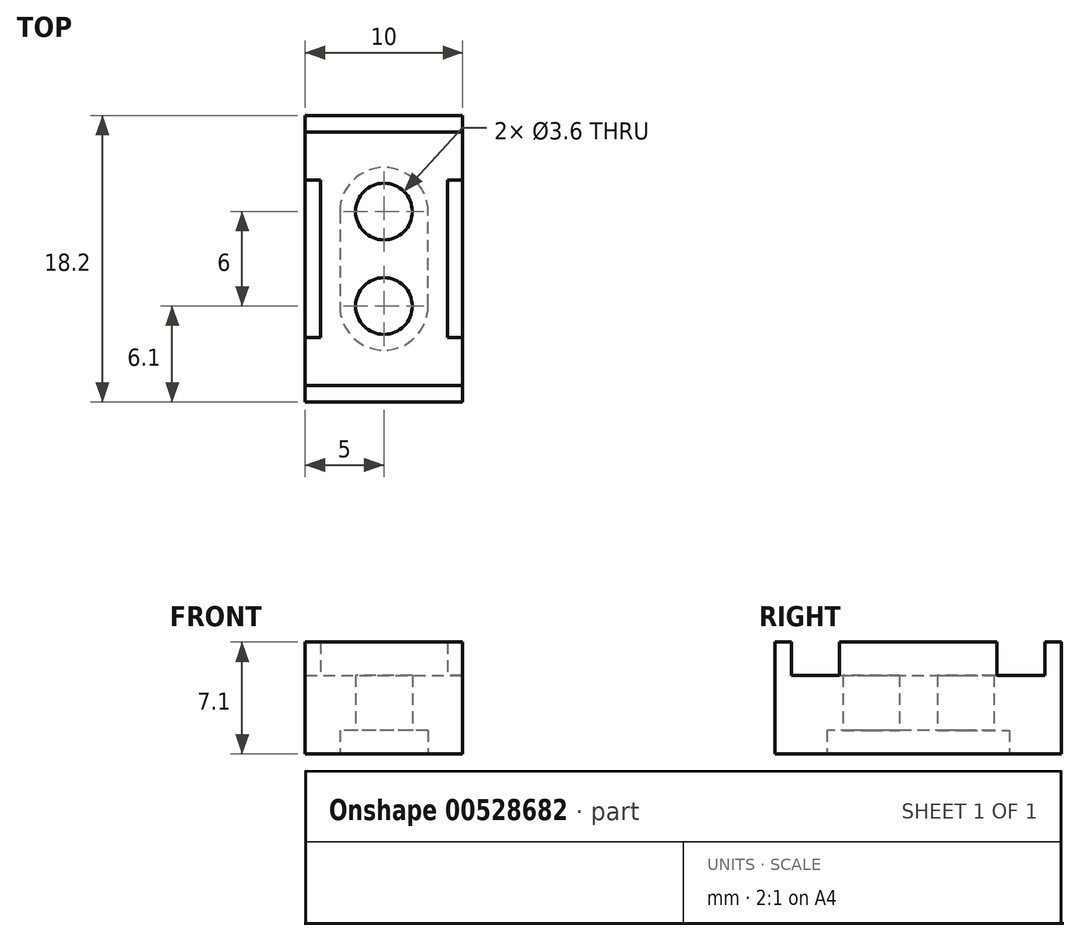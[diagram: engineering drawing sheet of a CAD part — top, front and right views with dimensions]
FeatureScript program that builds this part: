
annotation { "Feature Type Name" : "Feature", "Feature Type Description" : "" }
export const myFeature = defineFeature(function(context is Context, id is Id, definition is map)
    precondition{}
    {
        {
            var Q0;
            Q0=qCreatedBy(makeId("Top.planeOp"),FACE);
            var sketch = newSketch(context, id + "F0", { "sketchPlane" : qUnion([Q0])});
            skLineSegment(sketch, "E0.bottom", {"start": v(5, 9.1) * mm, "end": v(-5, 9.1) * mm});
            skLineSegment(sketch, "E0.top", {"start": v(5, -9.1) * mm, "end": v(-5, -9.1) * mm});
            skLineSegment(sketch, "E0.left", {"start": v(5, 9.1) * mm, "end": v(5, -9.1) * mm});
            skLineSegment(sketch, "E0.right", {"start": v(-5, 9.1) * mm, "end": v(-5, -9.1) * mm});
            skPoint(sketch, "E0.middle", {"position": v(0, 0) * mm});
            skLineSegment(sketch, "E1", {"start": v(0, 0) * mm, "end": v(0, 3) * mm, "construction": true});
            skCircle(sketch, "E2", {"center": v(0, 3) * mm, "radius": 1.8 * mm});
            skArc(sketch, "E3", {"start": v(2.8, 3) * mm, "mid": v(0, 5.8) * mm, "end": v(-2.8, 3) * mm});
            skLineSegment(sketch, "E4", {"start": v(-2.8, 3) * mm, "end": v(-2.8, 0) * mm});
            skLineSegment(sketch, "E5", {"start": v(2.8, 3) * mm, "end": v(2.8, 0) * mm});
            skArc(sketch, "E6.MirrorCS", {"start": v(2.8, -3) * mm, "mid": v(0, -5.8) * mm, "end": v(-2.8, -3) * mm});
            skLineSegment(sketch, "E7.MirrorCS", {"start": v(-2.8, -3) * mm, "end": v(-2.8, 0) * mm});
            skLineSegment(sketch, "E8.MirrorCS", {"start": v(2.8, -3) * mm, "end": v(2.8, 0) * mm});
            skCircle(sketch, "E9.MirrorC", {"center": v(0, -3) * mm, "radius": 1.8 * mm});
            skLineSegment(sketch, "E10.bottom", {"start": v(4.03, 8.05) * mm, "end": v(-4.03, 8.05) * mm});
            skLineSegment(sketch, "E10.top", {"start": v(4.03, -8.05) * mm, "end": v(-4.03, -8.05) * mm});
            skLineSegment(sketch, "E10.left", {"start": v(4.03, 8.05) * mm, "end": v(4.03, -8.05) * mm});
            skLineSegment(sketch, "E10.right", {"start": v(-4.03, 8.05) * mm, "end": v(-4.03, -8.05) * mm});
            skLineSegment(sketch, "E11", {"start": v(0, 0) * mm, "end": v(0, -5) * mm, "construction": true});
            skLineSegment(sketch, "E12", {"start": v(-4.03, -8.05) * mm, "end": v(-5, -8.05) * mm});
            skLineSegment(sketch, "E13", {"start": v(-4.03, -5) * mm, "end": v(-5, -5) * mm});
            skLineSegment(sketch, "E14.MirrorCS", {"start": v(4.03, -8.05) * mm, "end": v(5, -8.05) * mm});
            skLineSegment(sketch, "E15.MirrorCS", {"start": v(4.03, -5) * mm, "end": v(5, -5) * mm});
            skLineSegment(sketch, "E16.MirrorCS", {"start": v(4.03, 5) * mm, "end": v(5, 5) * mm});
            skLineSegment(sketch, "E17.MirrorCS", {"start": v(4.03, 8.05) * mm, "end": v(5, 8.05) * mm});
            skLineSegment(sketch, "E18.MirrorCS", {"start": v(-4.03, 5) * mm, "end": v(-5, 5) * mm});
            skLineSegment(sketch, "E19.MirrorCS", {"start": v(-4.03, 8.05) * mm, "end": v(-5, 8.05) * mm});
            skSolve(sketch);
        }
        {
            var Q0;
            {var subQ1=sQuery(id+"F0.wireOp",EDGE,"E0.top");Q0=makeQuery(id+"F0.imprint","IMPRINT",FACE,{"disambiguationData":[TD([[makeQuery(id+"F0.imprint","IMPRINT",EDGE,{"derivedFrom":subQ1}),-1.0]])]});}
            var Q1;
            {var subQ0=sQuery(id+"F0.wireOp",EDGE,"E14.MirrorCS");Q1=makeQuery(id+"F0.imprint","IMPRINT",FACE,{"disambiguationData":[TD([[makeQuery(id+"F0.imprint","IMPRINT",EDGE,{"derivedFrom":subQ0}),1.0]])]});}
            var Q2;
            Q2=makeQuery(id+"F0.imprint","IMPRINT",FACE,{"disambiguationData":[TD([[makeQuery(id+"F0.imprint","IMPRINT",EDGE,{"derivedFrom":sQuery(id+"F0.wireOp",EDGE,"E3")}),-1.0]])]});
            var Q3;
            {var subQ0=sQuery(id+"F0.wireOp",EDGE,"E12");Q3=makeQuery(id+"F0.imprint","IMPRINT",FACE,{"disambiguationData":[TD([[makeQuery(id+"F0.imprint","IMPRINT",EDGE,{"derivedFrom":subQ0}),-1.0]])]});}
            var Q4;
            {var subQ2=sQuery(id+"F0.wireOp",EDGE,"E13");Q4=makeQuery(id+"F0.imprint","IMPRINT",FACE,{"disambiguationData":[TD([[makeQuery(id+"F0.imprint","IMPRINT",EDGE,{"derivedFrom":subQ2}),-1.0]])]});}
            var Q5;
            {var subQ2=sQuery(id+"F0.wireOp",EDGE,"E15.MirrorCS");Q5=makeQuery(id+"F0.imprint","IMPRINT",FACE,{"disambiguationData":[TD([[makeQuery(id+"F0.imprint","IMPRINT",EDGE,{"derivedFrom":subQ2}),1.0]])]});}
            var Q6;
            {var subQ0=sQuery(id+"F0.wireOp",EDGE,"E16.MirrorCS");Q6=makeQuery(id+"F0.imprint","IMPRINT",FACE,{"disambiguationData":[TD([[makeQuery(id+"F0.imprint","IMPRINT",EDGE,{"derivedFrom":subQ0}),1.0]])]});}
            var Q7;
            {var subQ1=sQuery(id+"F0.wireOp",EDGE,"E0.bottom");Q7=makeQuery(id+"F0.imprint","IMPRINT",FACE,{"disambiguationData":[TD([[makeQuery(id+"F0.imprint","IMPRINT",EDGE,{"derivedFrom":subQ1}),1.0]])]});}
            var Q8;
            Q8=makeQuery(id+"F0.imprint","IMPRINT",FACE,{"disambiguationData":[TD([[makeQuery(id+"F0.imprint","IMPRINT",EDGE,{"derivedFrom":sQuery(id+"F0.wireOp",EDGE,"E2")}),-1.0]])]});
            var Q9;
            {var subQ0=sQuery(id+"F0.wireOp",EDGE,"E18.MirrorCS");Q9=makeQuery(id+"F0.imprint","IMPRINT",FACE,{"disambiguationData":[TD([[makeQuery(id+"F0.imprint","IMPRINT",EDGE,{"derivedFrom":subQ0}),-1.0]])]});}
            extrude(context, id + "F1", {"entities" : qUnion([Q0, Q1, Q2, Q3, Q4, Q5, Q6, Q7, Q8, Q9]), "depth" : 5 * mm, "offsetDistance" : 25 * mm});
        }
        {
            var Q0;
            Q0=makeQuery(id+"F0.imprint","IMPRINT",FACE,{"disambiguationData":[TD([[makeQuery(id+"F0.imprint","IMPRINT",EDGE,{"derivedFrom":sQuery(id+"F0.wireOp",EDGE,"E2")}),-1.0]])]});
            extrude(context, id + "F2", {"entities" : qUnion([Q0]), "operationType" : NewBodyOperationType.REMOVE, "depth" : 1.5 * mm, "offsetDistance" : 25 * mm});
        }
        {
            var Q0;
            {var subQ2=sQuery(id+"F0.wireOp",EDGE,"E13");Q0=makeQuery(id+"F0.imprint","IMPRINT",FACE,{"disambiguationData":[TD([[makeQuery(id+"F0.imprint","IMPRINT",EDGE,{"derivedFrom":subQ2}),-1.0]])]});}
            var Q1;
            {var subQ1=sQuery(id+"F0.wireOp",EDGE,"E0.top");Q1=makeQuery(id+"F0.imprint","IMPRINT",FACE,{"disambiguationData":[TD([[makeQuery(id+"F0.imprint","IMPRINT",EDGE,{"derivedFrom":subQ1}),-1.0]])]});}
            var Q2;
            {var subQ2=sQuery(id+"F0.wireOp",EDGE,"E15.MirrorCS");Q2=makeQuery(id+"F0.imprint","IMPRINT",FACE,{"disambiguationData":[TD([[makeQuery(id+"F0.imprint","IMPRINT",EDGE,{"derivedFrom":subQ2}),1.0]])]});}
            var Q3;
            {var subQ1=sQuery(id+"F0.wireOp",EDGE,"E0.bottom");Q3=makeQuery(id+"F0.imprint","IMPRINT",FACE,{"disambiguationData":[TD([[makeQuery(id+"F0.imprint","IMPRINT",EDGE,{"derivedFrom":subQ1}),1.0]])]});}
            extrude(context, id + "F3", {"entities" : qUnion([Q0, Q1, Q2, Q3]), "operationType" : NewBodyOperationType.ADD, "depth" : 7.1 * mm, "offsetDistance" : 25 * mm});
        }
    });
